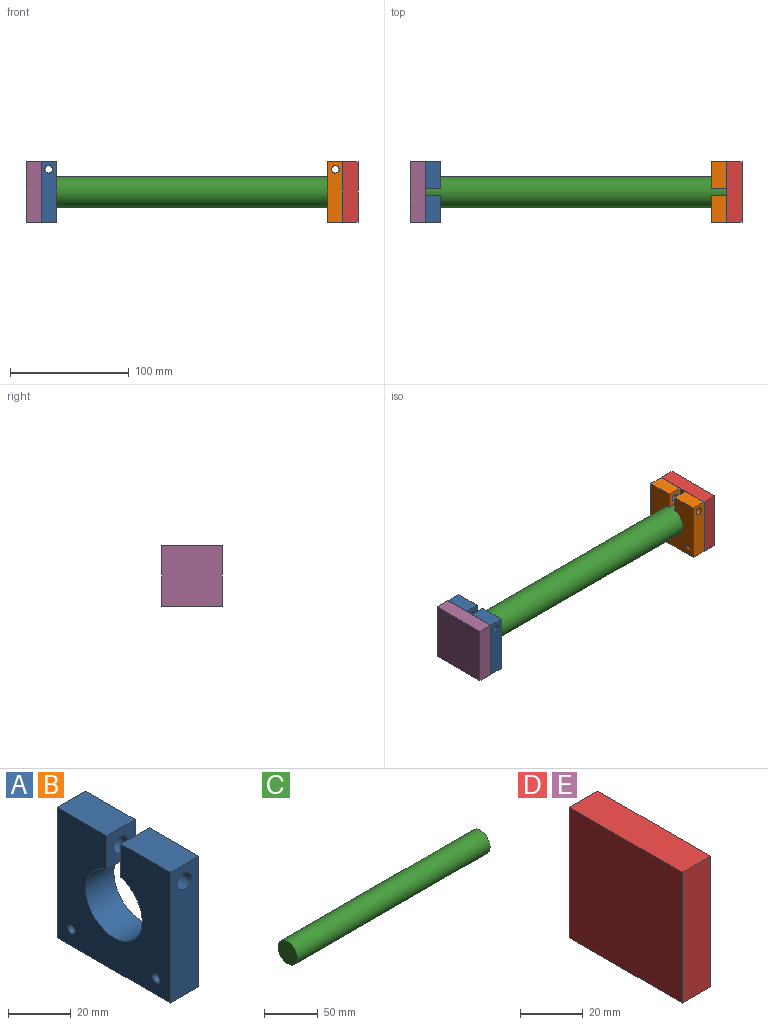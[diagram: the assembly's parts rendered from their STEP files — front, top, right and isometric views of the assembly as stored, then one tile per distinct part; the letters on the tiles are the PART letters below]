
ASSEMBLY  parts=5 mates=4
PART A: 14 faces, bbox 12.7x50.8x50.8 mm
  f0: plane 13.1x12.7mm, normal (0,-1,0), area 134.7mm2, adj f1,f9,f10,f11,f13
  f1: cylinder r=12.7mm len=25.4mm, axis (-1,0,0), area 931.9mm2, adj f0,f2,f10,f11
  f2: plane 13.1x12.7mm, normal (0,1,0), area 134.7mm2, adj f1,f3,f10,f11,f12
  f3: plane 22.23x12.7mm, normal (0,0,1), area 282.3mm2, adj f2,f4,f10,f11
  f4: plane 50.8x12.7mm, normal (0,-1,0), area 613.5mm2, adj f3,f5,f10,f11,f12
  f5: plane 50.8x12.7mm, normal (0,0,-1), area 645.2mm2, adj f4,f6,f10,f11
  f6: plane 50.8x12.7mm, normal (0,1,0), area 613.5mm2, adj f5,f9,f10,f11,f13
  f7: cylinder r=1.59mm len=12.7mm, axis (-1,0,0), area 126.7mm2, adj f10,f11
  f8: cylinder r=1.59mm len=12.7mm, axis (-1,0,0), area 126.7mm2, adj f10,f11
  f9: plane 22.23x12.7mm, normal (0,0,1), area 282.3mm2, adj f0,f6,f10,f11
  f10: plane 50.8x50.8mm, normal (1,0,0), area 1976.6mm2, adj f0,f1,f2,f3,f4,f5,f6,f7
  f11: plane 50.8x50.8mm, normal (-1,0,0), area 1976.6mm2, adj f0,f1,f2,f3,f4,f5,f6,f7
  f12: cylinder r=3.17mm len=22.23mm, axis (0,1,0), area 443.4mm2, adj f2,f4
  f13: cylinder r=3.17mm len=22.23mm, axis (0,1,0), area 443.4mm2, adj f0,f6
PART B: same geometry as A
PART C: 3 faces, bbox 254x25.4x25.4 mm
  f0: cylinder r=12.7mm len=254mm, axis (-1,0,0), area 20268.3mm2, adj f1,f2
  f1: plane 25.4x25.4mm, normal (1,0,0), area 506.7mm2, adj f0
  f2: plane 25.4x25.4mm, normal (-1,0,0), area 506.7mm2, adj f0
PART D: 6 faces, bbox 12.7x50.8x50.8 mm
  f0: plane 50.8x12.7mm, normal (0,1,0), area 645.2mm2, adj f1,f3,f4,f5
  f1: plane 50.8x12.7mm, normal (0,0,1), area 645.2mm2, adj f0,f2,f4,f5
  f2: plane 50.8x12.7mm, normal (0,-1,0), area 645.2mm2, adj f1,f3,f4,f5
  f3: plane 50.8x12.7mm, normal (0,0,-1), area 645.2mm2, adj f0,f2,f4,f5
  f4: plane 50.8x50.8mm, normal (1,0,0), area 2580.6mm2, adj f0,f1,f2,f3
  f5: plane 50.8x50.8mm, normal (-1,0,0), area 2580.6mm2, adj f0,f1,f2,f3
PART E: same geometry as D
PLACE A t=(-52.12,51.75,-33.33)mm
PLACE B t=(189.18,51.75,-33.33)mm
PLACE C t=(-52.12,51.75,-33.33)mm
PLACE D t=(201.88,51.75,-33.33)mm
PLACE E t=(-64.82,51.75,-33.33)mm
MATE fastened B.f10 <-> D.f5  axis (1,0,0) through (62.18,-43.5,42.87)mm
MATE revolute C.f0 <-> E.f4  axis (-1,0,0) through (-191.82,-68.9,68.27)mm
MATE revolute D.f5 <-> C.f0  axis (-1,0,0) through (62.18,-68.9,68.27)mm
MATE fastened A.f11 <-> E.f4  axis (-1,0,0) through (-191.82,-94.3,42.87)mm
